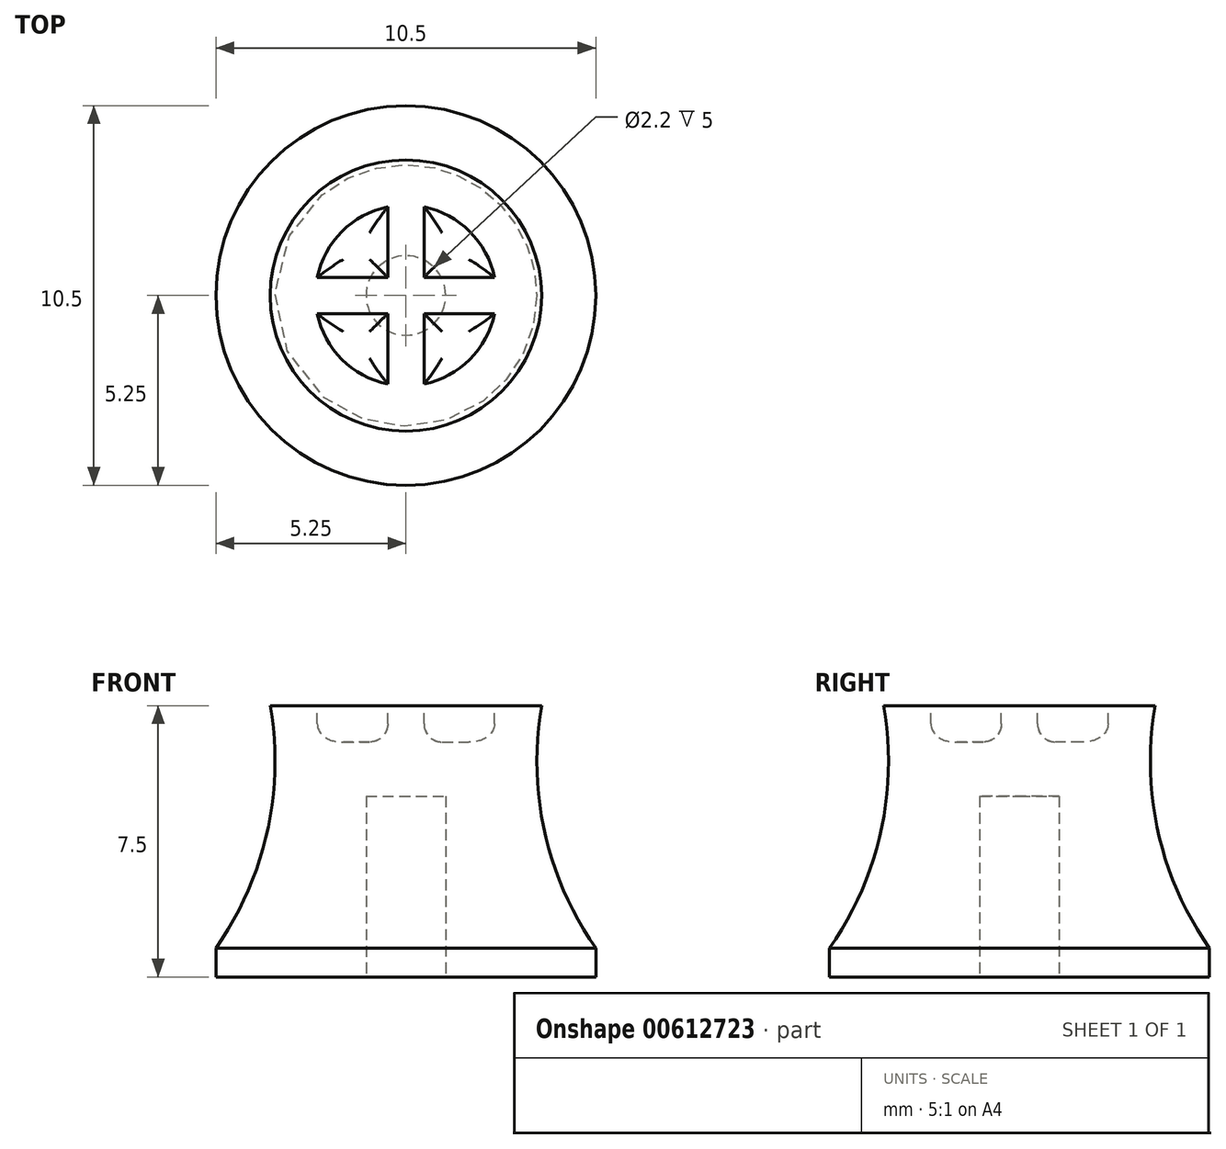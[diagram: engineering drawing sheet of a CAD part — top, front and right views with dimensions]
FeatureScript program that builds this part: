
annotation { "Feature Type Name" : "Feature", "Feature Type Description" : "" }
export const myFeature = defineFeature(function(context is Context, id is Id, definition is map)
    precondition{}
    {
        {
            var Q0;
            Q0=qCreatedBy(makeId("Right.planeOp"),FACE);
            var sketch = newSketch(context, id + "F0", { "sketchPlane" : qUnion([Q0])});
            skLineSegment(sketch, "E0", {"start": v(0, 0) * mm, "end": v(-5.25, 0) * mm});
            skLineSegment(sketch, "E1", {"start": v(0, 0) * mm, "end": v(0, 7.5) * mm});
            skLineSegment(sketch, "E2", {"start": v(0, 7.5) * mm, "end": v(-3.75, 7.5) * mm});
            skLineSegment(sketch, "E3", {"start": v(0, 24.51) * mm, "end": v(0, -9.99) * mm, "construction": true});
            skLineSegment(sketch, "E4", {"start": v(-5.25, 0) * mm, "end": v(-5.25, 0.8) * mm});
            skArc(sketch, "E5", {"start": v(-5.25, 0.8) * mm, "mid": v(-3.84, 4) * mm, "end": v(-3.75, 7.5) * mm});
            skSolve(sketch);
        }
        {
            var Q0;
            Q0=qSketchRegion(id+"F0",true);
            var Q1;
            Q1=sQuery(id+"F0.wireOp",EDGE,"E3");
            revolve(context, id + "F1", {"entities" : qUnion([Q0]), "axis" : qUnion([Q1]), "revolveType" : RevolveType.FULL});
        }
        {
            var Q0;
            Q0=makeQuery(id+"F1.opRevolve","SWEPT_FACE",FACE,{"disambiguationData":[OSD([sQuery(id+"F0.wireOp",EDGE,"E0")])]});
            var sketch = newSketch(context, id + "F2", { "sketchPlane" : qUnion([Q0])});
            skCircle(sketch, "E6", {"center": v(0, 0) * mm, "radius": 1.1 * mm});
            skSolve(sketch);
        }
        {
            var Q0;
            Q0=qSketchRegion(id+"F2",true);
            extrude(context, id + "F3", {"entities" : qUnion([Q0]), "operationType" : NewBodyOperationType.REMOVE, "oppositeDirection" : true, "depth" : 5 * mm, "offsetDistance" : 25 * mm});
        }
        {
            var Q0;
            Q0=makeQuery(id+"F1.opRevolve","SWEPT_FACE",FACE,{"disambiguationData":[OSD([sQuery(id+"F0.wireOp",EDGE,"E2")])]});
            var sketch = newSketch(context, id + "F4", { "sketchPlane" : qUnion([Q0])});
            skArc(sketch, "E7", {"start": v(-0.5, 2.45) * mm, "mid": v(-1.77, 1.77) * mm, "end": v(-2.45, 0.5) * mm});
            skLineSegment(sketch, "E8", {"start": v(0.5, 2.45) * mm, "end": v(0.5, 0.5) * mm});
            skLineSegment(sketch, "E9", {"start": v(-0.5, 2.45) * mm, "end": v(-0.5, 0.5) * mm});
            skLineSegment(sketch, "E10", {"start": v(-2.45, 0.5) * mm, "end": v(-0.5, 0.5) * mm});
            skLineSegment(sketch, "E11", {"start": v(-2.45, -0.5) * mm, "end": v(-0.5, -0.5) * mm});
            skArc(sketch, "E12.trimOffspring", {"start": v(-2.45, -0.5) * mm, "mid": v(-1.77, -1.77) * mm, "end": v(-0.5, -2.45) * mm});
            skArc(sketch, "E13.trimOffspring", {"start": v(0.5, -2.45) * mm, "mid": v(1.77, -1.77) * mm, "end": v(2.45, -0.5) * mm});
            skArc(sketch, "E14.trimOffspring", {"start": v(2.45, 0.5) * mm, "mid": v(1.77, 1.77) * mm, "end": v(0.5, 2.45) * mm});
            skLineSegment(sketch, "E15.trimOffspring", {"start": v(0.5, -0.5) * mm, "end": v(0.5, -2.45) * mm});
            skLineSegment(sketch, "E16.trimOffspring", {"start": v(0.5, 0.5) * mm, "end": v(2.45, 0.5) * mm});
            skLineSegment(sketch, "E17.trimOffspring", {"start": v(-0.5, -0.5) * mm, "end": v(-0.5, -2.45) * mm});
            skLineSegment(sketch, "E18.trimOffspring", {"start": v(0.5, -0.5) * mm, "end": v(2.45, -0.5) * mm});
            skSolve(sketch);
        }
        {
            var Q0;
            Q0=qSketchRegion(id+"F4",true);
            extrude(context, id + "F5", {"entities" : qUnion([Q0]), "operationType" : NewBodyOperationType.REMOVE, "oppositeDirection" : true, "depth" : 1 * mm, "offsetDistance" : 25 * mm});
        }
        {
            var Q0;
            Q0=makeQuery(id+"F5.boolean.opBoolean","COPY",FACE,{"derivedFrom":makeQuery(id+"F5.opExtrude","CAP_FACE",FACE,{"disambiguationData":[OSD([sQuery(id+"F4.wireOp",EDGE,"E7"),sQuery(id+"F4.wireOp",EDGE,"E9"),sQuery(id+"F4.wireOp",EDGE,"E10")])],"isStart":false})});
            var Q1;
            Q1=makeQuery(id+"F5.boolean.opBoolean","COPY",FACE,{"derivedFrom":makeQuery(id+"F5.opExtrude","CAP_FACE",FACE,{"disambiguationData":[OSD([sQuery(id+"F4.wireOp",EDGE,"E8"),sQuery(id+"F4.wireOp",EDGE,"E14.trimOffspring"),sQuery(id+"F4.wireOp",EDGE,"E16.trimOffspring")])],"isStart":false})});
            var Q2;
            Q2=makeQuery(id+"F5.boolean.opBoolean","COPY",FACE,{"derivedFrom":makeQuery(id+"F5.opExtrude","CAP_FACE",FACE,{"disambiguationData":[OSD([sQuery(id+"F4.wireOp",EDGE,"E13.trimOffspring"),sQuery(id+"F4.wireOp",EDGE,"E15.trimOffspring"),sQuery(id+"F4.wireOp",EDGE,"E18.trimOffspring")])],"isStart":false})});
            var Q3;
            Q3=makeQuery(id+"F5.boolean.opBoolean","COPY",FACE,{"derivedFrom":makeQuery(id+"F5.opExtrude","CAP_FACE",FACE,{"disambiguationData":[OSD([sQuery(id+"F4.wireOp",EDGE,"E11"),sQuery(id+"F4.wireOp",EDGE,"E12.trimOffspring"),sQuery(id+"F4.wireOp",EDGE,"E17.trimOffspring")])],"isStart":false})});
            fillet(context, id + "F6", {"entities" : qUnion([Q0, Q1, Q2, Q3]), "radius" : 0.5 * mm, "tangentPropagation" : true, "allowEdgeOverflow" : false});
        }
    });
